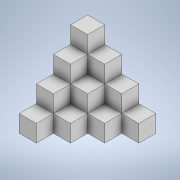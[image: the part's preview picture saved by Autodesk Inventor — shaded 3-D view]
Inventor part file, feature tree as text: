
AUTODESK INVENTOR PART (.ipt)
format: ipt  version: 2020 (Build 240168000, 168)  size: 178,688 bytes
history: native  units: mm
features: sketch x3, other x2, extrude x2, shell x1
ambient origin geometry x8: Origin, YZ Plane, XZ Plane, XY Plane, X Axis, Y Axis, Z Axis, Center Point
bodies: Solid1 (feature_tree)
feature tree (8):
  other  "Annotations"
  extrude  "Extrusion1"  Depth=20.0mm TaperAngle=0.0deg
  extrude  "Extrusion2"  Depth=20.0mm
  shell  "Shell1"  Thickness=20.0mm
  sketch  "Sketch1"  dims[d10=20.0mm d11=0.0mm d12=20.0mm d13=0.0mm]
  sketch  "Sketch2"  dims[d18=4.0mm d19=20.0mm d20=20.0mm]
  sketch  "Sketch4"  dims[d21=20.0mm d22=20.0mm d23=20.0mm d24=20.0mm d25=20.0mm d26=20.0mm d27=20.0mm d31=20.0mm d32=0.0mm d33=20.0mm d34=0.0mm d35=3.572223mm d36=3.765028mm d37=4.0mm]
  other  "Linear Dimension 1"
